# Revit family: KEUCO_59592010001
name_source: partatom
category: Allgemeines Modell
revit_build: Autodesk Revit 2016 (Build: 20150220_1215(x64)
units: mm (PartAtom-declared; Revit-internal decimal feet)

## family parameters
Arbeitsebenenbasiert = Ja
Beim Laden mit Abzugskörper schneiden = Nein
Bemaßung runder Anschluss = Durchmesser verwenden
Gemeinsam genutzt = Nein
Immer vertikal = Nein
Kann Basisbauteil für Bewehrung sein = Nein
Raumberechnungspunkt = Nein
Teiletyp = Normal

## types (1)
- 59592010001
    Artikelnummer = 59592010001
    Ausschreibungstext = KEUCO IXMO Schlauchanschluss mit Brausehalter DN15, 59592010001
Schlauchanschluss aus hochglanzverchromten Messing
mit runder Rosette und integriertem Brausehalter für Schläuche 
mit konischer Mutter, z.B. KEUCO Brauseschlauch 54995..., 
eigensicher gegen Rückfließen, frei positionierbar,
Rosettendurchmesser 90 mm, Stärke 10 mm, 
Schlauchanschluss G 1/2 Zoll, Gesamtausladung 55 mm
    Beschreibung = für Schläuche mit konischer Mutter
mit runder Rosette, eigensicher gegen Rückfließen
nach DIN EN 1717
    Breite = 45 mm  [stored 0.147638 ft]
    Gewicht = 0
    Hersteller = KEUCO
    Material = Stahl, verchromt
    Serie = Plan
    URL = https://www.keuco.com
    Verwendung = DU / WA
    Vorgabe-Ansicht = 1219 mm

note: [stored X ft] marks values corroborated as IEEE doubles in the binary element streams (Revit-internal decimal feet)

## geometry (parser evidence)
native form markers: Sweep x3
no freeform markers — native parametric forms only
